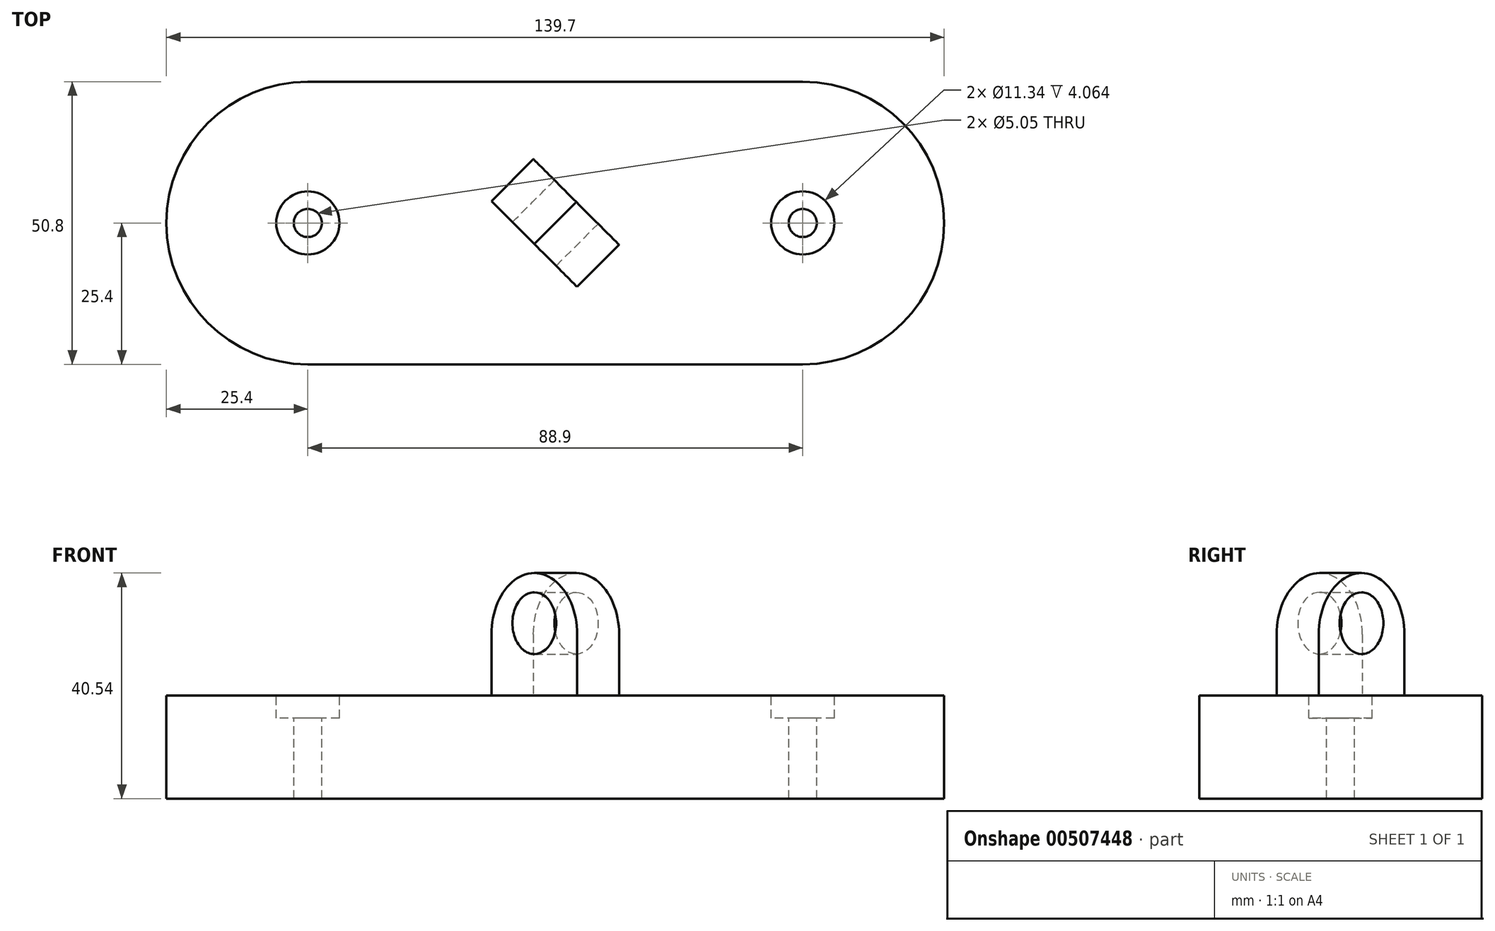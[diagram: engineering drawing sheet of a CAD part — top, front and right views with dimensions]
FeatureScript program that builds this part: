
annotation { "Feature Type Name" : "Feature", "Feature Type Description" : "" }
export const myFeature = defineFeature(function(context is Context, id is Id, definition is map)
    precondition{}
    {
        {
            var Q0;
            Q0=qCreatedBy(makeId("Top.planeOp"),FACE);
            var sketch = newSketch(context, id + "F0", { "sketchPlane" : qUnion([Q0])});
            skLineSegment(sketch, "E0.bottom", {"start": v(-44.45, 25.4) * mm, "end": v(44.45, 25.4) * mm});
            skLineSegment(sketch, "E0.top", {"start": v(-44.45, -25.4) * mm, "end": v(44.45, -25.4) * mm});
            skPoint(sketch, "E0.middle", {"position": v(0, 0) * mm});
            skArc(sketch, "E1", {"start": v(-44.45, 25.4) * mm, "mid": v(-69.85, 0) * mm, "end": v(-44.45, -25.4) * mm});
            skArc(sketch, "E2", {"start": v(44.45, 25.4) * mm, "mid": v(69.85, 0) * mm, "end": v(44.45, -25.4) * mm});
            skSolve(sketch);
        }
        {
            var Q0;
            Q0=makeQuery(id+"F0.imprint","IMPRINT",FACE,{"disambiguationData":[TD([[makeQuery(id+"F0.imprint","IMPRINT",EDGE,{"derivedFrom":sQuery(id+"F0.wireOp",EDGE,"E0.bottom")}),-1.0]])]});
            extrude(context, id + "F1", {"entities" : qUnion([Q0]), "depth" : 18.54 * mm});
        }
        {
            var Q0;
            Q0=makeQuery(id+"F1.opExtrude","CAP_FACE",FACE,{"disambiguationData":[OSD([sQuery(id+"F0.wireOp",EDGE,"E0.bottom"),sQuery(id+"F0.wireOp",EDGE,"E0.top"),sQuery(id+"F0.wireOp",EDGE,"E1"),sQuery(id+"F0.wireOp",EDGE,"E2")])],"isStart":false});
            var sketch = newSketch(context, id + "F2", { "sketchPlane" : qUnion([Q0])});
            skCircle(sketch, "E3", {"center": v(44.45, 0) * mm, "radius": 5.67 * mm});
            skCircle(sketch, "E4", {"center": v(-44.45, 0) * mm, "radius": 5.67 * mm});
            skSolve(sketch);
        }
        {
            var Q0;
            Q0=makeQuery(id+"F2.imprint","IMPRINT",FACE,{"disambiguationData":[TD([[makeQuery(id+"F2.imprint","IMPRINT",EDGE,{"derivedFrom":sQuery(id+"F2.wireOp",EDGE,"E4")}),1.0]])]});
            var Q1;
            Q1=makeQuery(id+"F2.imprint","IMPRINT",FACE,{"disambiguationData":[TD([[makeQuery(id+"F2.imprint","IMPRINT",EDGE,{"derivedFrom":sQuery(id+"F2.wireOp",EDGE,"E3")}),1.0]])]});
            extrude(context, id + "F3", {"entities" : qUnion([Q0, Q1]), "operationType" : NewBodyOperationType.REMOVE, "oppositeDirection" : true, "depth" : 4.06 * mm});
        }
        {
            var Q0;
            Q0=makeQuery(id+"F1.opExtrude","CAP_FACE",FACE,{"disambiguationData":[OSD([sQuery(id+"F0.wireOp",EDGE,"E0.bottom"),sQuery(id+"F0.wireOp",EDGE,"E0.top"),sQuery(id+"F0.wireOp",EDGE,"E1"),sQuery(id+"F0.wireOp",EDGE,"E2")])],"isStart":false});
            var sketch = newSketch(context, id + "F4", { "sketchPlane" : qUnion([Q0])});
            skCircle(sketch, "E5", {"center": v(-44.45, 0) * mm, "radius": 2.52 * mm});
            skCircle(sketch, "E6", {"center": v(44.45, 0) * mm, "radius": 2.52 * mm});
            skSolve(sketch);
        }
        {
            var Q0;
            Q0=makeQuery(id+"F4.imprint","IMPRINT",FACE,{"disambiguationData":[TD([[makeQuery(id+"F4.imprint","IMPRINT",EDGE,{"derivedFrom":sQuery(id+"F4.wireOp",EDGE,"E5")}),1.0]])]});
            var Q1;
            Q1=makeQuery(id+"F4.imprint","IMPRINT",FACE,{"disambiguationData":[TD([[makeQuery(id+"F4.imprint","IMPRINT",EDGE,{"derivedFrom":sQuery(id+"F4.wireOp",EDGE,"E6")}),1.0]])]});
            extrude(context, id + "F5", {"entities" : qUnion([Q0, Q1]), "operationType" : NewBodyOperationType.REMOVE, "endBound" : BoundingType.THROUGH_ALL, "oppositeDirection" : true, "depth" : 25.4 * mm});
        }
        {
            var Q0;
            Q0=qCreatedBy(makeId("Front.planeOp"),FACE);
            var sketch = newSketch(context, id + "F6", { "sketchPlane" : qUnion([Q0])});
            skLineSegment(sketch, "E7", {"start": v(0, 0) * mm, "end": v(0, 51.62) * mm, "construction": true});
            skSolve(sketch);
        }
        {
            var Q0;
            Q0=sQuery(id+"F6.wireOp",EDGE,"E7");
            cPlane(context, id + "F7", {"entities" : qUnion([Q0]), "cplaneType" : CPlaneType.LINE_ANGLE, "offset" : 25.4 * mm, "angle" : 45 * degree, "width" : 152.4 * mm, "height" : 152.4 * mm});
        }
        {
            var Q0;
            Q0=qCreatedBy(id+"F7.planeOp",FACE);
            var sketch = newSketch(context, id + "F8", { "sketchPlane" : qUnion([Q0])});
            skLineSegment(sketch, "E8.bottom", {"start": v(-10.89, 40.55) * mm, "end": v(10.89, 40.55) * mm});
            skPoint(sketch, "E8.middle", {"position": v(0, 0) * mm});
            skPoint(sketch, "E8.left.end.orphan", {"position": v(-10.89, -40.55) * mm});
            skPoint(sketch, "E8.right.end.orphan", {"position": v(10.89, -40.55) * mm});
            skLineSegment(sketch, "E9", {"start": v(10.89, 40.55) * mm, "end": v(10.89, 0) * mm});
            skLineSegment(sketch, "E10", {"start": v(-10.89, 40.55) * mm, "end": v(-10.89, 0) * mm});
            skLineSegment(sketch, "E11", {"start": v(-10.89, 0) * mm, "end": v(10.89, 0) * mm});
            skSolve(sketch);
        }
        {
            var Q0;
            Q0 = qSketchRegion(id + "F8", true);
            var Q1;
            Q1=makeQuery(id+"F8.imprint","IMPRINT",FACE,{"disambiguationData":[TD([[makeQuery(id+"F8.imprint","IMPRINT",EDGE,{"derivedFrom":sQuery(id+"F8.wireOp",EDGE,"E8.bottom")}),-1.0]])]});
            extrude(context, id + "F9", {"entities" : qUnion([Q0, Q1]), "operationType" : NewBodyOperationType.ADD, "endBound" : BoundingType.SYMMETRIC, "depth" : 10.67 * mm});
        }
        {
            var Q0;
            Q0=makeQuery(id+"F9.opExtrude","SWEPT_EDGE",EDGE,{"disambiguationData":[OSD([sQuery(id+"F8.wireOp",EDGE,"E8.bottom"),sQuery(id+"F8.wireOp",EDGE,"E10")])]});
            var Q1;
            Q1=makeQuery(id+"F9.opExtrude","SWEPT_EDGE",EDGE,{"disambiguationData":[OSD([sQuery(id+"F8.wireOp",EDGE,"E8.bottom"),sQuery(id+"F8.wireOp",EDGE,"E9")])]});
            fillet(context, id + "F10", {"entities" : qUnion([Q0, Q1]), "radius" : 11.04 * mm, "tangentPropagation" : true, "allowEdgeOverflow" : false});
        }
        {
            var Q0;
            Q0=makeQuery(id+"F9.opExtrude","CAP_FACE",FACE,{"disambiguationData":[OSD([sQuery(id+"F8.wireOp",EDGE,"E8.bottom"),sQuery(id+"F8.wireOp",EDGE,"E9"),sQuery(id+"F8.wireOp",EDGE,"E10"),sQuery(id+"F8.wireOp",EDGE,"E11")])],"isStart":false});
            var sketch = newSketch(context, id + "F11", { "sketchPlane" : qUnion([Q0])});
            skCircle(sketch, "E12", {"center": v(0, 31.53) * mm, "radius": 5.55 * mm});
            skSolve(sketch);
        }
        {
            var Q0;
            Q0 = qSketchRegion(id + "F11", true);
            extrude(context, id + "F12", {"entities" : qUnion([Q0]), "operationType" : NewBodyOperationType.REMOVE, "endBound" : BoundingType.THROUGH_ALL, "oppositeDirection" : true, "depth" : 25.4 * mm});
        }
    });
